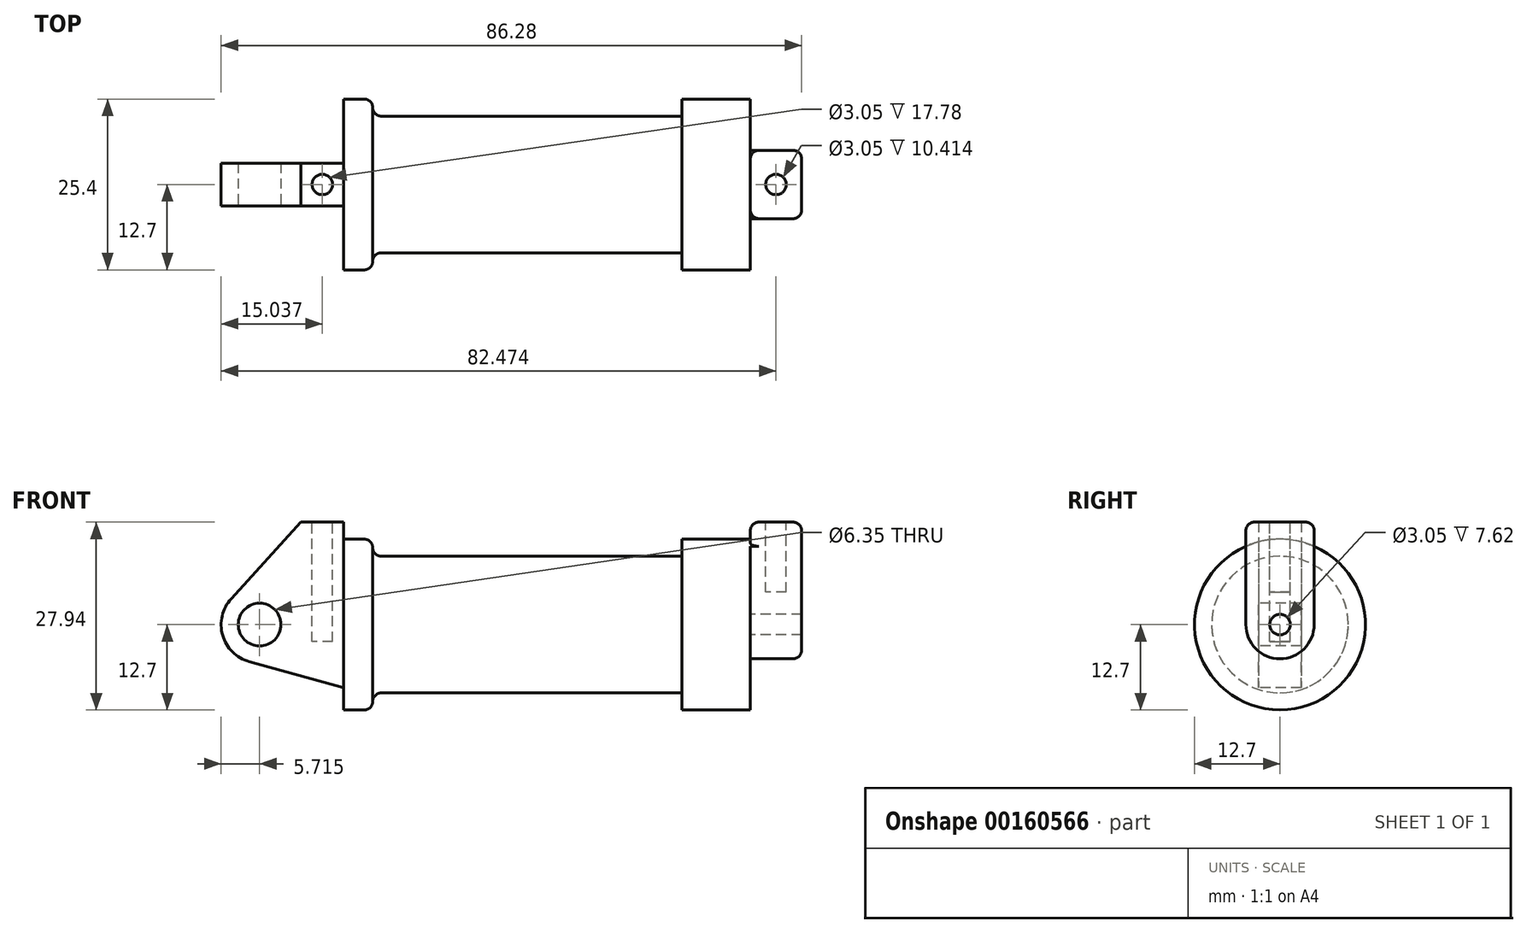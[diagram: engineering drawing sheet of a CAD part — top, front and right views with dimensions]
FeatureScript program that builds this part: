
annotation { "Feature Type Name" : "Feature", "Feature Type Description" : "" }
export const myFeature = defineFeature(function(context is Context, id is Id, definition is map)
    precondition{}
    {
        {
            var Q0;
            Q0=qCreatedBy(makeId("Front.planeOp"),FACE);
            var sketch = newSketch(context, id + "F0", { "sketchPlane" : qUnion([Q0])});
            skLineSegment(sketch, "E0", {"start": v(0, 0) * mm, "end": v(0, 12.7) * mm});
            skLineSegment(sketch, "E1", {"start": v(0, 12.7) * mm, "end": v(10.16, 12.7) * mm});
            skLineSegment(sketch, "E2", {"start": v(10.16, 12.7) * mm, "end": v(10.16, 10.16) * mm});
            skLineSegment(sketch, "E3", {"start": v(10.16, 10.16) * mm, "end": v(56.13, 10.16) * mm});
            skLineSegment(sketch, "E4", {"start": v(56.13, 10.16) * mm, "end": v(56.13, 12.7) * mm});
            skLineSegment(sketch, "E5", {"start": v(56.13, 12.7) * mm, "end": v(66.3, 12.7) * mm});
            skLineSegment(sketch, "E6", {"start": v(66.3, 12.7) * mm, "end": v(66.3, 0) * mm});
            skLineSegment(sketch, "E7", {"start": v(66.3, 0) * mm, "end": v(0, 0) * mm});
            skLineSegment(sketch, "E8", {"start": v(5.84, 15.24) * mm, "end": v(-0.5, 15.24) * mm});
            skLineSegment(sketch, "E9", {"start": v(-0.5, 15.24) * mm, "end": v(-10.88, 3.85) * mm});
            skLineSegment(sketch, "E10", {"start": v(0, 0) * mm, "end": v(-6.65, 0) * mm});
            skCircle(sketch, "E11", {"center": v(-6.65, 0) * mm, "radius": 5.72 * mm});
            skCircle(sketch, "E12", {"center": v(-6.65, 0) * mm, "radius": 3.18 * mm});
            skLineSegment(sketch, "E13", {"start": v(5.84, 15.24) * mm, "end": v(5.84, -9.4) * mm});
            skLineSegment(sketch, "E14", {"start": v(5.84, -9.4) * mm, "end": v(-8.18, -5.5) * mm});
            skSolve(sketch);
        }
        {
            var Q0;
            {var subQ0=sQuery(id+"F0.wireOp",EDGE,"E2");Q0=makeQuery(id+"F0.imprint","IMPRINT",FACE,{"disambiguationData":[TD([[makeQuery(id+"F0.imprint","IMPRINT",EDGE,{"derivedFrom":subQ0}),-1.0]])]});}
            var Q1;
            Q1=sQuery(id+"F0.wireOp",EDGE,"E7");
            revolve(context, id + "F1", {"entities" : qUnion([Q0]), "axis" : qUnion([Q1]), "revolveType" : RevolveType.FULL});
        }
        {
            var Q0;
            {var subQ0=sQuery(id+"F0.wireOp",EDGE,"E14");Q0=makeQuery(id+"F0.imprint","IMPRINT",FACE,{"disambiguationData":[TD([[makeQuery(id+"F0.imprint","IMPRINT",EDGE,{"derivedFrom":subQ0}),-1.0]])]});}
            var Q1;
            {var subQ3=sQuery(id+"F0.wireOp",EDGE,"E0");Q1=makeQuery(id+"F0.imprint","IMPRINT",FACE,{"disambiguationData":[TD([[makeQuery(id+"F0.imprint","IMPRINT",EDGE,{"derivedFrom":subQ3}),1.0]])]});}
            var Q2;
            {var subQ0=sQuery(id+"F0.wireOp",EDGE,"E0");Q2=makeQuery(id+"F0.imprint","IMPRINT",FACE,{"disambiguationData":[TD([[makeQuery(id+"F0.imprint","IMPRINT",EDGE,{"derivedFrom":subQ0}),-1.0]])]});}
            var Q3;
            {var subQ4=sQuery(id+"F0.wireOp",EDGE,"E12");Q3=makeQuery(id+"F0.imprint","IMPRINT",FACE,{"disambiguationData":[TD([[makeQuery(id+"F0.imprint","IMPRINT",EDGE,{"derivedFrom":subQ4}),-1.0]])]});}
            extrude(context, id + "F2", {"entities" : qUnion([Q0, Q1, Q2, Q3]), "operationType" : NewBodyOperationType.ADD, "endBound" : BoundingType.SYMMETRIC, "oppositeDirection" : true, "depth" : 6.35 * mm});
        }
        {
            var Q0;
            Q0=makeQuery(id+"F1.opRevolve","SWEPT_FACE",FACE,{"disambiguationData":[OSD([sQuery(id+"F0.wireOp",EDGE,"E6")])]});
            var sketch = newSketch(context, id + "F3", { "sketchPlane" : qUnion([Q0])});
            skCircle(sketch, "E15", {"center": v(0, 0) * mm, "radius": 1.52 * mm});
            skCircle(sketch, "E16", {"center": v(0, 0) * mm, "radius": 5.08 * mm});
            skLineSegment(sketch, "E17", {"start": v(-5.08, 0) * mm, "end": v(-5.08, 15.24) * mm});
            skLineSegment(sketch, "E18", {"start": v(5.08, 0) * mm, "end": v(5.08, 15.24) * mm});
            skLineSegment(sketch, "E19", {"start": v(-5.08, 15.24) * mm, "end": v(5.08, 15.24) * mm});
            skSolve(sketch);
        }
        {
            var Q0;
            Q0 = qSketchRegion(id + "F3", true);
            extrude(context, id + "F4", {"entities" : qUnion([Q0]), "operationType" : NewBodyOperationType.ADD, "depth" : 7.62 * mm});
        }
        {
            var Q0;
            Q0=makeQuery(id+"F2.opExtrude","SWEPT_FACE",FACE,{"disambiguationData":[OSD([sQuery(id+"F0.wireOp",EDGE,"E8")])]});
            var sketch = newSketch(context, id + "F5", { "sketchPlane" : qUnion([Q0])});
            skCircle(sketch, "E20", {"center": v(2.67, 0) * mm, "radius": 1.52 * mm});
            skPoint(sketch, "E20.centerSnap0", {"position": v(2.67, -3.18) * mm});
            skPoint(sketch, "E20.centerSnap1", {"position": v(-0.5, 0) * mm});
            skSolve(sketch);
        }
        {
            var Q0;
            Q0=makeQuery(id+"F4.opExtrude","SWEPT_FACE",FACE,{"disambiguationData":[OSD([sQuery(id+"F3.wireOp",EDGE,"E19")])]});
            var sketch = newSketch(context, id + "F6", { "sketchPlane" : qUnion([Q0])});
            skCircle(sketch, "E21", {"center": v(70.1, 0) * mm, "radius": 1.52 * mm});
            skPoint(sketch, "E21.centerSnap0", {"position": v(70.1, -5.08) * mm});
            skPoint(sketch, "E21.centerSnap1", {"position": v(66.3, 0) * mm});
            skSolve(sketch);
        }
        {
            var Q0;
            Q0 = qSketchRegion(id + "F5", true);
            extrude(context, id + "F7", {"entities" : qUnion([Q0]), "operationType" : NewBodyOperationType.REMOVE, "oppositeDirection" : true, "depth" : 17.78 * mm});
        }
        {
            var Q0;
            Q0 = qSketchRegion(id + "F6", true);
            extrude(context, id + "F8", {"entities" : qUnion([Q0]), "operationType" : NewBodyOperationType.REMOVE, "oppositeDirection" : true, "depth" : 10.4 * mm});
        }
        {
            var Q0;
            Q0=makeQuery(id+"F1.opRevolve","SWEPT_EDGE",EDGE,{"disambiguationData":[OSD([sQuery(id+"F0.wireOp",EDGE,"E1"),sQuery(id+"F0.wireOp",EDGE,"E2")])]});
            var Q1;
            Q1=makeQuery(id+"F1.opRevolve","SWEPT_EDGE",EDGE,{"disambiguationData":[OSD([sQuery(id+"F0.wireOp",EDGE,"E2"),sQuery(id+"F0.wireOp",EDGE,"E3")])]});
            fillet(context, id + "F9", {"entities" : qUnion([Q0, Q1]), "radius" : 1.27 * mm, "tangentPropagation" : true, "allowEdgeOverflow" : false});
        }
        {
            var Q0;
            {var subQ0=sQuery(id+"F3.wireOp",EDGE,"E17");Q0=makeQuery(id+"F4.boolean.opBoolean","SPLIT",EDGE,{"disambiguationData":[topologyDisambiguationEdgeConnected([makeQuery(id+"F1.opRevolve","SWEPT_FACE",FACE,{"disambiguationData":[OSD([sQuery(id+"F0.wireOp",EDGE,"E6")])]})])],"derivedFrom":makeQuery(id+"F4.opExtrude","CAP_EDGE",EDGE,{"disambiguationData":[OSD([subQ0])],"isStart":true})});}
            var Q1;
            {var subQ0=sQuery(id+"F3.wireOp",EDGE,"E18");Q1=makeQuery(id+"F4.boolean.opBoolean","SPLIT",EDGE,{"disambiguationData":[topologyDisambiguationEdgeConnected([makeQuery(id+"F1.opRevolve","SWEPT_FACE",FACE,{"disambiguationData":[OSD([sQuery(id+"F0.wireOp",EDGE,"E6")])]})])],"derivedFrom":makeQuery(id+"F4.opExtrude","CAP_EDGE",EDGE,{"disambiguationData":[OSD([subQ0])],"isStart":true})});}
            var Q2;
            Q2=makeQuery(id+"F4.opExtrude","CAP_EDGE",EDGE,{"disambiguationData":[OSD([sQuery(id+"F3.wireOp",EDGE,"E18")])],"isStart":false});
            var Q3;
            Q3=makeQuery(id+"F4.opExtrude","CAP_EDGE",EDGE,{"disambiguationData":[OSD([sQuery(id+"F3.wireOp",EDGE,"E17")])],"isStart":false});
            var Q4;
            Q4=makeQuery(id+"F4.opExtrude","CAP_EDGE",EDGE,{"disambiguationData":[OSD([sQuery(id+"F3.wireOp",EDGE,"E19")])],"isStart":false});
            var Q5;
            Q5=makeQuery(id+"F4.opExtrude","CAP_EDGE",EDGE,{"disambiguationData":[OSD([sQuery(id+"F3.wireOp",EDGE,"E19")])],"isStart":true});
            var Q6;
            Q6=makeQuery(id+"F4.opExtrude","SWEPT_EDGE",EDGE,{"disambiguationData":[OSD([sQuery(id+"F3.wireOp",EDGE,"E18"),sQuery(id+"F3.wireOp",EDGE,"E19")])]});
            var Q7;
            Q7=makeQuery(id+"F4.opExtrude","SWEPT_EDGE",EDGE,{"disambiguationData":[OSD([sQuery(id+"F3.wireOp",EDGE,"E17"),sQuery(id+"F3.wireOp",EDGE,"E19")])]});
            var Q8;
            Q8=makeQuery(id+"F4.opExtrude","CAP_EDGE",EDGE,{"disambiguationData":[OSD([sQuery(id+"F3.wireOp",EDGE,"E16")])],"isStart":false});
            var Q9;
            Q9=makeQuery(id+"F4.opExtrude","CAP_EDGE",EDGE,{"disambiguationData":[OSD([sQuery(id+"F3.wireOp",EDGE,"E16")])],"isStart":true});
            fillet(context, id + "F10", {"entities" : qUnion([Q0, Q1, Q2, Q3, Q4, Q5, Q6, Q7, Q8, Q9]), "radius" : 1.27 * mm, "tangentPropagation" : true, "allowEdgeOverflow" : false});
        }
    });
